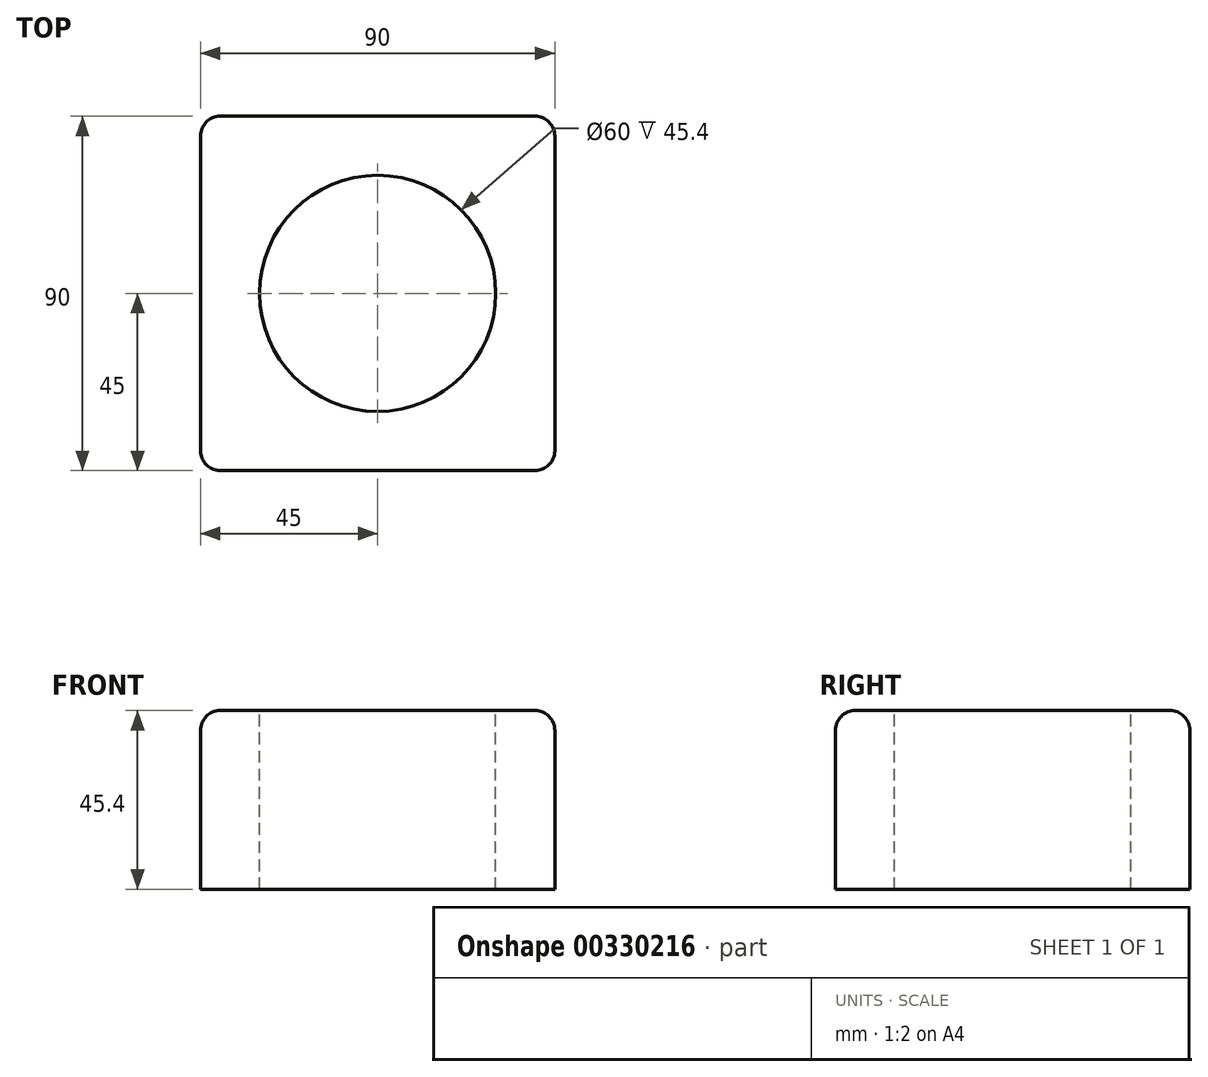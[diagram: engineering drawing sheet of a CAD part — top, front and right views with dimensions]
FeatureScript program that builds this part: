
annotation { "Feature Type Name" : "Feature", "Feature Type Description" : "" }
export const myFeature = defineFeature(function(context is Context, id is Id, definition is map)
    precondition{}
    {
        {
            var Q0;
            Q0=qCreatedBy(makeId("Top.planeOp"),FACE);
            var sketch = newSketch(context, id + "F0", { "sketchPlane" : qUnion([Q0])});
            skLineSegment(sketch, "E0.bottom", {"start": v(-45, 45) * mm, "end": v(45, 45) * mm});
            skLineSegment(sketch, "E0.top", {"start": v(-45, -45) * mm, "end": v(45, -45) * mm});
            skLineSegment(sketch, "E0.left", {"start": v(-45, 45) * mm, "end": v(-45, -45) * mm});
            skLineSegment(sketch, "E0.right", {"start": v(45, 45) * mm, "end": v(45, -45) * mm});
            skPoint(sketch, "E0.middle", {"position": v(0, 0) * mm});
            skSolve(sketch);
        }
        {
            var Q0;
            Q0=makeQuery(id+"F0.imprint","IMPRINT",FACE,{"disambiguationData":[TD([[makeQuery(id+"F0.imprint","IMPRINT",EDGE,{"derivedFrom":sQuery(id+"F0.wireOp",EDGE,"E0.bottom")}),-1.0]])]});
            extrude(context, id + "F1", {"entities" : qUnion([Q0]), "depth" : 45.4 * mm});
        }
        {
            var Q0;
            Q0=makeQuery(id+"F1.opExtrude","CAP_FACE",FACE,{"disambiguationData":[OSD([sQuery(id+"F0.wireOp",EDGE,"E0.bottom"),sQuery(id+"F0.wireOp",EDGE,"E0.top"),sQuery(id+"F0.wireOp",EDGE,"E0.left"),sQuery(id+"F0.wireOp",EDGE,"E0.right")])],"isStart":false});
            var sketch = newSketch(context, id + "F2", { "sketchPlane" : qUnion([Q0])});
            skCircle(sketch, "E1", {"center": v(0, 0) * mm, "radius": 30 * mm});
            skSolve(sketch);
        }
        {
            var Q0;
            Q0=makeQuery(id+"F2.imprint","IMPRINT",FACE,{"disambiguationData":[TD([[makeQuery(id+"F2.imprint","IMPRINT",EDGE,{"derivedFrom":sQuery(id+"F2.wireOp",EDGE,"E1")}),1.0]])]});
            extrude(context, id + "F3", {"entities" : qUnion([Q0]), "operationType" : NewBodyOperationType.REMOVE, "endBound" : BoundingType.THROUGH_ALL, "oppositeDirection" : true, "depth" : 25 * mm});
        }
        {
            var Q0;
            Q0=makeQuery(id+"F1.opExtrude","SWEPT_EDGE",EDGE,{"disambiguationData":[OSD([sQuery(id+"F0.wireOp",EDGE,"E0.bottom"),sQuery(id+"F0.wireOp",EDGE,"E0.left")])]});
            var Q1;
            Q1=makeQuery(id+"F1.opExtrude","SWEPT_EDGE",EDGE,{"disambiguationData":[OSD([sQuery(id+"F0.wireOp",EDGE,"E0.top"),sQuery(id+"F0.wireOp",EDGE,"E0.left")])]});
            var Q2;
            Q2=makeQuery(id+"F1.opExtrude","SWEPT_EDGE",EDGE,{"disambiguationData":[OSD([sQuery(id+"F0.wireOp",EDGE,"E0.bottom"),sQuery(id+"F0.wireOp",EDGE,"E0.right")])]});
            var Q3;
            Q3=makeQuery(id+"F1.opExtrude","CAP_EDGE",EDGE,{"disambiguationData":[OSD([sQuery(id+"F0.wireOp",EDGE,"E0.right")])],"isStart":false});
            var Q4;
            Q4=makeQuery(id+"F1.opExtrude","CAP_EDGE",EDGE,{"disambiguationData":[OSD([sQuery(id+"F0.wireOp",EDGE,"E0.left")])],"isStart":false});
            var Q5;
            Q5=makeQuery(id+"F1.opExtrude","CAP_EDGE",EDGE,{"disambiguationData":[OSD([sQuery(id+"F0.wireOp",EDGE,"E0.bottom")])],"isStart":false});
            var Q6;
            Q6=makeQuery(id+"F1.opExtrude","CAP_EDGE",EDGE,{"disambiguationData":[OSD([sQuery(id+"F0.wireOp",EDGE,"E0.top")])],"isStart":false});
            fillet(context, id + "F4", {"entities" : qUnion([Q0, Q1, Q2, Q3, Q4, Q5, Q6]), "radius" : 5 * mm, "tangentPropagation" : true, "allowEdgeOverflow" : false});
        }
        {
            var Q0;
            Q0=makeQuery(id+"F1.opExtrude","SWEPT_EDGE",EDGE,{"disambiguationData":[OSD([sQuery(id+"F0.wireOp",EDGE,"E0.top"),sQuery(id+"F0.wireOp",EDGE,"E0.right")])]});
            fillet(context, id + "F5", {"entities" : qUnion([Q0]), "radius" : 5 * mm, "tangentPropagation" : true, "allowEdgeOverflow" : false});
        }
    });
